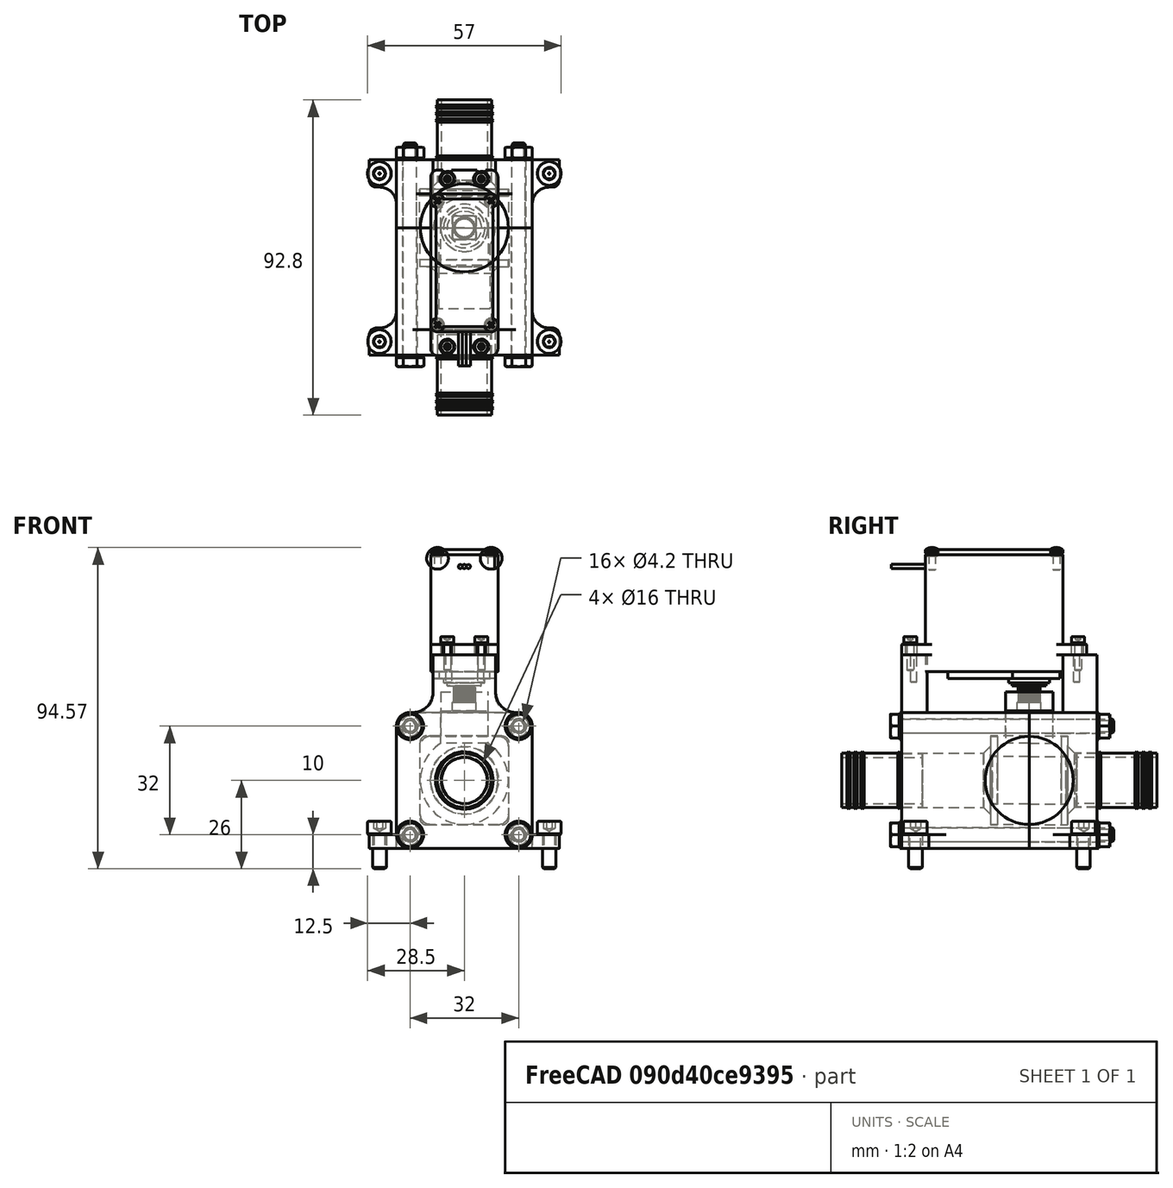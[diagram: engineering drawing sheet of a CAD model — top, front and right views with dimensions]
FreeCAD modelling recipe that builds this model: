
FCSTD DOCUMENT  (FreeCAD 0.19R20655 (Git))
Label: servo_valve_assembly
License: All rights reserved
LicenseURL: http://en.wikipedia.org/wiki/All_rights_reserved
objects: Part::FeaturePython×42
note: 42 computed .brp shape members not serialized (recipe doc carries the construction recipe); baked Part::Feature solids carry a one-line shape summary decoded from their .brp

FEATURE [Part::FeaturePython] b_ball_001_  label="ball_001"  # a2plus imported part (geometry in sourceFile) (typed FeaturePython)
  a2p_Version = V0.1
  fixedPosition = true
  objectType = a2pPart
  sourceFile = .\ball.FCStd
  subassemblyImport = false
  timeLastImport = 1.58808e+09
  updateColors = true
FEATURE [Part::FeaturePython] b_ball_001_001  label="ball_002"  # a2plus imported part (geometry in sourceFile) (typed FeaturePython)
  Placement = pos=(0,0,0) rot=(0,0,1;3.14159rad)
  a2p_Version = V0.1
  fixedPosition = true
  objectType = a2pPart
  sourceFile = .\ball.FCStd
  subassemblyImport = false
  timeLastImport = 1.58808e+09
  updateColors = true
FEATURE [Part::FeaturePython] b_coupling_001_  label="coupling_001"  # a2plus imported part (geometry in sourceFile) (typed FeaturePython)
  Placement = pos=(0,0,26) rot=(0,1,0;3.14159rad)
  a2p_Version = V0.1
  fixedPosition = false
  objectType = a2pPart
  sourceFile = .\coupling.FCStd
  subassemblyImport = false
  timeLastImport = 1.58808e+09
  updateColors = true
FEATURE [Part::FeaturePython] b_housing_left_001_  label="housing_left_001"  # a2plus imported part (geometry in sourceFile) (typed FeaturePython)
  Placement = pos=(0,20,-4.5585e-07) rot=(1,0,0;1.5708rad)
  a2p_Version = V0.1
  fixedPosition = false
  objectType = a2pPart
  sourceFile = .\housing_left.FCStd
  subassemblyImport = false
  timeLastImport = 1.58808e+09
  updateColors = true
FEATURE [Part::FeaturePython] b_housing_right_001_  label="housing_right_001"  # a2plus imported part (geometry in sourceFile) (typed FeaturePython)
  Placement = pos=(0,-37.5,4.77329e-07) rot=(0,0.707107,0.707107;3.14159rad)
  a2p_Version = V0.1
  fixedPosition = false
  objectType = a2pPart
  sourceFile = .\housing_right.FCStd
  subassemblyImport = false
  timeLastImport = 1.58808e+09
  updateColors = true
FEATURE [Part::FeaturePython] b_servo_001_  label="servo_001"  # a2plus imported part (geometry in sourceFile) (typed FeaturePython)
  Placement = pos=(-9e-14,7.26708e-07,68) rot=(0.707107,0.707107,0;3.14159rad)
  a2p_Version = V0.1
  fixedPosition = true
  objectType = a2pPart
  sourceFile = .\servo.FCStd
  subassemblyImport = false
  timeLastImport = 1.58808e+09
  updateColors = true
FEATURE [Part::FeaturePython] b_gasket_001_  label="gasket_001"  # a2plus imported part (geometry in sourceFile) (typed FeaturePython)
  Placement = pos=(0,9.40001,-2e-15) rot=(-1,0,0;1.5708rad)
  a2p_Version = V0.1
  fixedPosition = false
  objectType = a2pPart
  sourceFile = .\gasket.FCStd
  subassemblyImport = false
  timeLastImport = 1.58808e+09
  updateColors = true
FEATURE [Part::FeaturePython] b_gasket_001_001  label="gasket_002"  # a2plus imported part (geometry in sourceFile) (typed FeaturePython)
  Placement = pos=(0,-11.4,-1.10767e-07) rot=(-1,0,0;1.5708rad)
  a2p_Version = V0.1
  fixedPosition = false
  objectType = a2pPart
  sourceFile = .\gasket.FCStd
  subassemblyImport = false
  timeLastImport = 1.58808e+09
  updateColors = true
FEATURE [Part::FeaturePython] b_hose_connector_001_  label="hose_connector_001"  # a2plus imported part (geometry in sourceFile) (typed FeaturePython)
  Placement = pos=(0,-31.5,3.40351e-07) rot=(1,0,0;1.5708rad)
  a2p_Version = V0.1
  fixedPosition = false
  objectType = a2pPart
  sourceFile = .\hose_connector.FCStd
  subassemblyImport = false
  timeLastImport = 1.58808e+09
  updateColors = true
FEATURE [Part::FeaturePython] b_hose_connector_001_001  label="hose_connector_002"  # a2plus imported part (geometry in sourceFile) (typed FeaturePython)
  Placement = pos=(0,14,-5.29607e-07) rot=(-1,0,0;1.5708rad)
  a2p_Version = V0.1
  fixedPosition = false
  objectType = a2pPart
  sourceFile = .\hose_connector.FCStd
  subassemblyImport = false
  timeLastImport = 1.58808e+09
  updateColors = true
FEATURE [Part::FeaturePython] Screw  label="M4x10-Screw"  # Fasteners workbench fastener (typed FeaturePython)
  Placement = pos=(25,16,-16) rot=(0,0,1;0rad)
  baseObject = -> b_housing_left_001_ [Edge256]
  diameter = 5
  invert = false
  length = 11
  lengthCustom = 10
  matchOuter = false
  offset = 0
  thread = false
  type = 16
FEATURE [Part::FeaturePython] Screw001  label="M4x10-Screw003"  # Fasteners workbench fastener (typed FeaturePython)
  Placement = pos=(-25,16,-16) rot=(0,0,1;0rad)
  baseObject = -> b_housing_left_001_ [Edge105]
  diameter = 5
  invert = false
  length = 11
  lengthCustom = 10
  matchOuter = false
  offset = 0
  thread = false
  type = 16
FEATURE [Part::FeaturePython] Screw002  label="M4x10-Screw001"  # Fasteners workbench fastener (typed FeaturePython)
  Placement = pos=(25,-33.5,-16) rot=(-1,0,0;0rad)
  baseObject = -> b_housing_right_001_ [Edge225]
  diameter = 5
  invert = false
  length = 11
  lengthCustom = 10
  matchOuter = false
  offset = 0
  thread = false
  type = 16
FEATURE [Part::FeaturePython] Screw003  label="M4x10-Screw002"  # Fasteners workbench fastener (typed FeaturePython)
  Placement = pos=(-25,-33.5,-16) rot=(-1,0,0;0rad)
  baseObject = -> b_housing_right_001_ [Edge118]
  diameter = 5
  invert = false
  length = 11
  lengthCustom = 10
  matchOuter = false
  offset = 0
  thread = false
  type = 16
FEATURE [Part::FeaturePython] Screw004  label="M2x5-Screw"  # Fasteners workbench fastener (typed FeaturePython)
  Placement = pos=(-7.9,-28.6,67) rot=(0,0,1;0rad)
  baseObject = -> b_servo_001_ [Edge78]
  diameter = 2
  invert = false
  length = 2
  lengthCustom = 5
  matchOuter = false
  offset = 0
  thread = false
  type = 17
FEATURE [Part::FeaturePython] Screw005  label="M2x5-Screw004"  # Fasteners workbench fastener (typed FeaturePython)
  Placement = pos=(7.9,-28.6,67) rot=(0,0,1;0rad)
  baseObject = -> b_servo_001_ [Edge186]
  diameter = 2
  invert = false
  length = 2
  lengthCustom = 5
  matchOuter = false
  offset = 0
  thread = false
  type = 17
FEATURE [Part::FeaturePython] Screw006  label="M2x5-Screw005"  # Fasteners workbench fastener (typed FeaturePython)
  Placement = pos=(7.9,8,67) rot=(0,0,1;0rad)
  baseObject = -> b_servo_001_ [Edge413]
  diameter = 2
  invert = false
  length = 2
  lengthCustom = 5
  matchOuter = false
  offset = 0
  thread = false
  type = 17
FEATURE [Part::FeaturePython] Screw007  label="M2x5-Screw006"  # Fasteners workbench fastener (typed FeaturePython)
  Placement = pos=(-7.9,8,67) rot=(0,0,1;0rad)
  baseObject = -> b_servo_001_ [Edge170]
  diameter = 2
  invert = false
  length = 2
  lengthCustom = 5
  matchOuter = false
  offset = 0
  thread = false
  type = 17
FEATURE [Part::FeaturePython] Washer  label="M4-Washer"  # Fasteners workbench fastener (typed FeaturePython)
  Placement = pos=(-16,20,16) rot=(-1,0,0;1.5708rad)
  baseObject = -> b_housing_left_001_ [Edge88]
  diameter = 5
  invert = true
  matchOuter = false
  offset = 0
  type = 2
FEATURE [Part::FeaturePython] Washer001  label="M4-Washer001"  # Fasteners workbench fastener (typed FeaturePython)
  Placement = pos=(16,20,16) rot=(-1,0,0;1.5708rad)
  baseObject = -> b_housing_left_001_ [Edge82]
  diameter = 5
  invert = true
  matchOuter = false
  offset = 0
  type = 2
FEATURE [Part::FeaturePython] Washer002  label="M4-Washer002"  # Fasteners workbench fastener (typed FeaturePython)
  Placement = pos=(-16,-37.5,16) rot=(1,0,0;1.5708rad)
  baseObject = -> b_housing_right_001_ [Edge70]
  diameter = 5
  invert = true
  matchOuter = false
  offset = 0
  type = 2
FEATURE [Part::FeaturePython] Washer003  label="M4-Washer003"  # Fasteners workbench fastener (typed FeaturePython)
  Placement = pos=(16,-37.5,16) rot=(1,0,0;1.5708rad)
  baseObject = -> b_housing_right_001_ [Edge76]
  diameter = 5
  invert = true
  matchOuter = false
  offset = 0
  type = 2
FEATURE [Part::FeaturePython] Washer004  label="M4-Washer004"  # Fasteners workbench fastener (typed FeaturePython)
  Placement = pos=(16,-37.5,-16) rot=(1,0,0;1.5708rad)
  baseObject = -> b_housing_right_001_ [Edge74]
  diameter = 5
  invert = true
  matchOuter = false
  offset = 0
  type = 2
FEATURE [Part::FeaturePython] Washer005  label="M4-Washer005"  # Fasteners workbench fastener (typed FeaturePython)
  Placement = pos=(-16,-37.5,-16) rot=(1,0,0;1.5708rad)
  baseObject = -> b_housing_right_001_ [Edge72]
  diameter = 5
  invert = true
  matchOuter = false
  offset = 0
  type = 2
FEATURE [Part::FeaturePython] Washer006  label="M4-Washer006"  # Fasteners workbench fastener (typed FeaturePython)
  Placement = pos=(16,20,-16) rot=(-1,0,0;1.5708rad)
  baseObject = -> b_housing_left_001_ [Edge84]
  diameter = 5
  invert = true
  matchOuter = false
  offset = 0
  type = 2
FEATURE [Part::FeaturePython] Washer007  label="M4-Washer007"  # Fasteners workbench fastener (typed FeaturePython)
  Placement = pos=(-16,20,-16) rot=(-1,0,0;1.5708rad)
  baseObject = -> b_housing_left_001_ [Edge86]
  diameter = 5
  invert = true
  matchOuter = false
  offset = 0
  type = 2
FEATURE [Part::FeaturePython] Nut  label="M4-Nut"  # Fasteners workbench fastener (typed FeaturePython)
  Placement = pos=(16,20.55,16) rot=(-1,0,0;1.5708rad)
  baseObject = -> Washer001 [Edge1]
  diameter = 6
  invert = false
  matchOuter = false
  offset = 0
  thread = false
  type = 4
FEATURE [Part::FeaturePython] Nut001  label="M4-Nut001"  # Fasteners workbench fastener (typed FeaturePython)
  Placement = pos=(-16,20.55,16) rot=(-1,0,0;1.5708rad)
  baseObject = -> Washer [Edge1]
  diameter = 6
  invert = false
  matchOuter = false
  offset = 0
  thread = false
  type = 4
FEATURE [Part::FeaturePython] Nut002  label="M4-Nut002"  # Fasteners workbench fastener (typed FeaturePython)
  Placement = pos=(16,20.55,-16) rot=(-1,0,0;1.5708rad)
  baseObject = -> Washer006 [Edge1]
  diameter = 6
  invert = false
  matchOuter = false
  offset = 0
  thread = false
  type = 4
FEATURE [Part::FeaturePython] Nut003  label="M4-Nut003"  # Fasteners workbench fastener (typed FeaturePython)
  Placement = pos=(-16,20.55,-16) rot=(-1,0,0;1.5708rad)
  baseObject = -> Washer007 [Edge1]
  diameter = 6
  invert = false
  matchOuter = false
  offset = 0
  thread = false
  type = 4
FEATURE [Part::FeaturePython] Screw008  label="M4x63-Screw"  # Fasteners workbench fastener (typed FeaturePython)
  Placement = pos=(16,-38.05,16) rot=(1,0,0;1.5708rad)
  baseObject = -> Washer003 [Edge1]
  diameter = 6
  invert = false
  length = 6
  lengthCustom = 63
  matchOuter = false
  offset = 0
  thread = false
  type = 14
FEATURE [Part::FeaturePython] Screw009  label="M4x63-Screw001"  # Fasteners workbench fastener (typed FeaturePython)
  Placement = pos=(-16,-38.05,16) rot=(1,0,0;1.5708rad)
  baseObject = -> Washer002 [Edge1]
  diameter = 6
  invert = false
  length = 6
  lengthCustom = 63
  matchOuter = false
  offset = 0
  thread = false
  type = 14
FEATURE [Part::FeaturePython] Screw010  label="M4x63-Screw003"  # Fasteners workbench fastener (typed FeaturePython)
  Placement = pos=(-16,-38.05,-16) rot=(1,0,0;1.5708rad)
  baseObject = -> Washer005 [Edge1]
  diameter = 6
  invert = false
  length = 6
  lengthCustom = 63
  matchOuter = false
  offset = 0
  thread = false
  type = 14
FEATURE [Part::FeaturePython] Screw011  label="M4x63-Screw002"  # Fasteners workbench fastener (typed FeaturePython)
  Placement = pos=(16,-38.05,-16) rot=(1,0,0;1.5708rad)
  baseObject = -> Washer004 [Edge1]
  diameter = 6
  invert = false
  length = 6
  lengthCustom = 63
  matchOuter = false
  offset = 0
  thread = false
  type = 14
FEATURE [Part::FeaturePython] Washer008  label="M2-Washer"  # Fasteners workbench fastener (typed FeaturePython)
  Placement = pos=(-5,-35,40) rot=(0,0,1;0rad)
  baseObject = -> b_servo_001_ [Edge103]
  diameter = 2
  invert = true
  matchOuter = false
  offset = 0
  type = 2
FEATURE [Part::FeaturePython] Washer009  label="M2-Washer001"  # Fasteners workbench fastener (typed FeaturePython)
  Placement = pos=(5,-35,40) rot=(0,0,1;0rad)
  baseObject = -> b_servo_001_ [Edge98]
  diameter = 2
  invert = true
  matchOuter = false
  offset = 0
  type = 2
FEATURE [Part::FeaturePython] Washer010  label="M2-Washer002"  # Fasteners workbench fastener (typed FeaturePython)
  Placement = pos=(5,14.4,40) rot=(0,0,1;0rad)
  baseObject = -> b_servo_001_ [Edge124]
  diameter = 2
  invert = true
  matchOuter = false
  offset = 0
  type = 2
FEATURE [Part::FeaturePython] Washer011  label="M2-Washer003"  # Fasteners workbench fastener (typed FeaturePython)
  Placement = pos=(-5,14.4,40) rot=(0,0,1;0rad)
  baseObject = -> b_servo_001_ [Edge347]
  diameter = 2
  invert = true
  matchOuter = false
  offset = 0
  type = 2
FEATURE [Part::FeaturePython] Screw012  label="M2x8-Screw"  # Fasteners workbench fastener (typed FeaturePython)
  Placement = pos=(-5,-35,40.35) rot=(0,0,1;0rad)
  baseObject = -> Washer008 [Edge1]
  diameter = 1
  invert = false
  length = 9
  lengthCustom = 8
  matchOuter = false
  offset = 0
  thread = false
  type = 6
FEATURE [Part::FeaturePython] Screw013  label="M2x8-Screw001"  # Fasteners workbench fastener (typed FeaturePython)
  Placement = pos=(5,-35,40.35) rot=(0,0,1;0rad)
  baseObject = -> Washer009 [Edge1]
  diameter = 1
  invert = false
  length = 9
  lengthCustom = 8
  matchOuter = false
  offset = 0
  thread = false
  type = 6
FEATURE [Part::FeaturePython] Screw014  label="M2x8-Screw002"  # Fasteners workbench fastener (typed FeaturePython)
  Placement = pos=(-5,14.4,40.35) rot=(0,0,1;0rad)
  baseObject = -> Washer011 [Edge1]
  diameter = 1
  invert = false
  length = 9
  lengthCustom = 8
  matchOuter = false
  offset = 0
  thread = false
  type = 6
FEATURE [Part::FeaturePython] Screw015  label="M2x8-Screw003"  # Fasteners workbench fastener (typed FeaturePython)
  Placement = pos=(5,14.4,40.35) rot=(0,0,1;0rad)
  baseObject = -> Washer010 [Edge1]
  diameter = 1
  invert = false
  length = 4
  lengthCustom = 8
  matchOuter = false
  offset = 0
  thread = false
  type = 6
